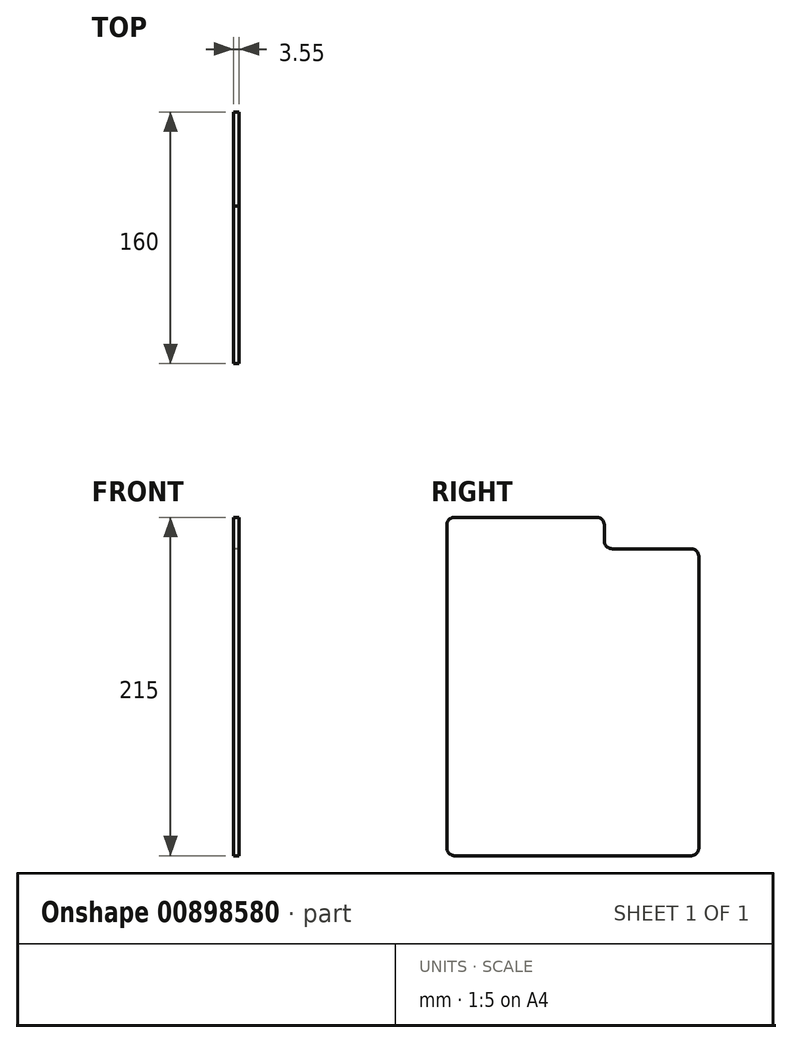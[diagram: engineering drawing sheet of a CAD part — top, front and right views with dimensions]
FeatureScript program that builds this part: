
annotation { "Feature Type Name" : "Feature", "Feature Type Description" : "" }
export const myFeature = defineFeature(function(context is Context, id is Id, definition is map)
    precondition{}
    {
        {
            var Q0;
            Q0=qCreatedBy(makeId("Right.planeOp"),FACE);
            var sketch = newSketch(context, id + "F0", { "sketchPlane" : qUnion([Q0])});
            skLineSegment(sketch, "E0.bottom", {"start": v(50, 107.5) * mm, "end": v(-50, 107.5) * mm});
            skLineSegment(sketch, "E0.top", {"start": v(50, -107.5) * mm, "end": v(-50, -107.5) * mm});
            skLineSegment(sketch, "E0.left", {"start": v(50, 107.5) * mm, "end": v(50, -107.5) * mm});
            skLineSegment(sketch, "E0.right", {"start": v(-50, 107.5) * mm, "end": v(-50, -107.5) * mm});
            skPoint(sketch, "E0.middle", {"position": v(0, 0) * mm});
            skLineSegment(sketch, "E1.bottom", {"start": v(50, -107.5) * mm, "end": v(110, -107.5) * mm});
            skLineSegment(sketch, "E1.top", {"start": v(50, 87.5) * mm, "end": v(110, 87.5) * mm});
            skLineSegment(sketch, "E1.left", {"start": v(50, -107.5) * mm, "end": v(50, 87.5) * mm});
            skLineSegment(sketch, "E1.right", {"start": v(110, -107.5) * mm, "end": v(110, 87.5) * mm});
            skSolve(sketch);
        }
        {
            var Q0;
            Q0 = qSketchRegion(id + "F0", true);
            extrude(context, id + "F1", {"entities" : qUnion([Q0]), "depth" : 3.55 * mm, "offsetDistance" : 25 * mm});
        }
        {
            var Q0;
            Q0=makeQuery(id+"F1.opExtrude","SWEPT_EDGE",EDGE,{"disambiguationData":[OSD([sQuery(id+"F0.wireOp",EDGE,"E0.left"),sQuery(id+"F0.wireOp",EDGE,"E1.top"),sQuery(id+"F0.wireOp",EDGE,"E1.left")])]});
            var Q1;
            Q1=makeQuery(id+"F1.opExtrude","SWEPT_EDGE",EDGE,{"disambiguationData":[OSD([sQuery(id+"F0.wireOp",EDGE,"E0.bottom"),sQuery(id+"F0.wireOp",EDGE,"E0.left")])]});
            var Q2;
            Q2=makeQuery(id+"F1.opExtrude","SWEPT_EDGE",EDGE,{"disambiguationData":[OSD([sQuery(id+"F0.wireOp",EDGE,"E1.top"),sQuery(id+"F0.wireOp",EDGE,"E1.right")])]});
            var Q3;
            Q3=makeQuery(id+"F1.opExtrude","SWEPT_EDGE",EDGE,{"disambiguationData":[OSD([sQuery(id+"F0.wireOp",EDGE,"E0.bottom"),sQuery(id+"F0.wireOp",EDGE,"E0.right")])]});
            var Q4;
            Q4=makeQuery(id+"F1.opExtrude","SWEPT_EDGE",EDGE,{"disambiguationData":[OSD([sQuery(id+"F0.wireOp",EDGE,"E1.bottom"),sQuery(id+"F0.wireOp",EDGE,"E1.right")])]});
            var Q5;
            Q5=makeQuery(id+"F1.opExtrude","SWEPT_EDGE",EDGE,{"disambiguationData":[OSD([sQuery(id+"F0.wireOp",EDGE,"E0.top"),sQuery(id+"F0.wireOp",EDGE,"E0.right")])]});
            fillet(context, id + "F2", {"entities" : qUnion([Q0, Q1, Q2, Q3, Q4, Q5]), "radius" : 5 * mm, "tangentPropagation" : true, "allowEdgeOverflow" : false});
        }
    });
